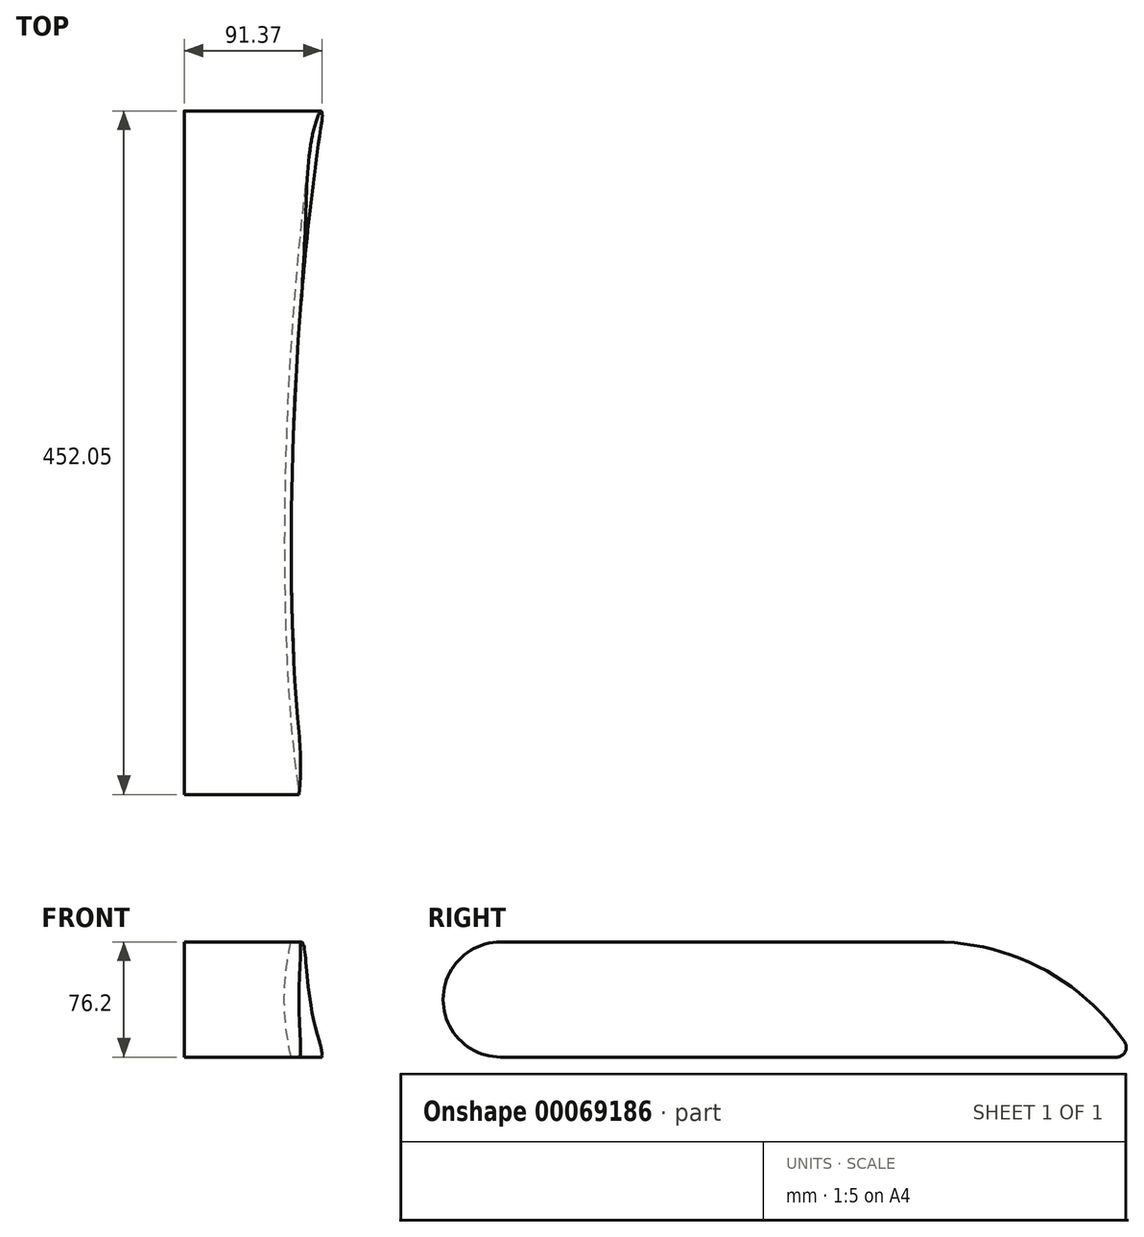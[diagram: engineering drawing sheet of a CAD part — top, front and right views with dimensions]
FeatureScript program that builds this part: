
annotation { "Feature Type Name" : "Feature", "Feature Type Description" : "" }
export const myFeature = defineFeature(function(context is Context, id is Id, definition is map)
    precondition{}
    {
        {
            var Q0;
            Q0=qCreatedBy(makeId("Right.planeOp"),FACE);
            var sketch = newSketch(context, id + "F0", { "sketchPlane" : qUnion([Q0])});
            skFitSpline(sketch, "E0", {"points": [v(0, 125.99) * mm, v(69.38, 151.55) * mm, v(311.86, 161.04) * mm, v(585.01, 131.83) * mm, v(681.42, 98.96) * mm, v(675.58, 90.93) * mm, v(579.9, 116.5) * mm, v(297.25, 149.36) * mm, v(127.81, 148.63) * mm, v(37.98, 131.1) * mm, v(0, 114.3) * mm, v(0, 125.99) * mm]});
            skLineSegment(sketch, "E1", {"start": v(0, 0) * mm, "end": v(154.83, 0) * mm, "construction": true});
            skSolve(sketch);
        }
        {
            var Q0;
            Q0=sQuery(id+"F0.wireOp",EDGE,"E0");
            var Q1;
            Q1=sQuery(id+"F0.wireOp",EDGE,"E1");
            revolve(context, id + "F1", {"bodyType" : ToolBodyType.SURFACE, "surfaceEntities" : qUnion([Q0]), "axis" : qUnion([Q1]), "revolveType" : RevolveType.FULL});
        }
        {
            var Q0;
            Q0=qCreatedBy(makeId("Right.planeOp"),FACE);
            cPlane(context, id + "F2", {"entities" : qUnion([Q0]), "cplaneType" : CPlaneType.OFFSET, "offset" : 228.6 * mm, "oppositeDirection" : true, "width" : 152.4 * mm, "height" : 152.4 * mm});
        }
        {
            var Q0;
            Q0=qCreatedBy(id+"F2.planeOp",FACE);
            var sketch = newSketch(context, id + "F3", { "sketchPlane" : qUnion([Q0])});
            skLineSegment(sketch, "E2.bottom", {"start": v(76.2, 38.1) * mm, "end": v(533.4, 38.1) * mm});
            skLineSegment(sketch, "E2.top", {"start": v(76.2, -38.1) * mm, "end": v(533.4, -38.1) * mm});
            skLineSegment(sketch, "E2.left", {"start": v(76.2, 38.1) * mm, "end": v(76.2, -38.1) * mm});
            skLineSegment(sketch, "E2.right", {"start": v(533.4, 38.1) * mm, "end": v(533.4, -38.1) * mm});
            skSolve(sketch);
        }
        {
            var Q0;
            Q0=makeQuery(id+"F3.imprint","IMPRINT",FACE,{"disambiguationData":[TD([[makeQuery(id+"F3.imprint","IMPRINT",EDGE,{"derivedFrom":sQuery(id+"F3.wireOp",EDGE,"E2.bottom")}),-1.0]])]});
            var Q1;
            Q1=makeQuery(id+"F1.opRevolve","SWEPT_FACE",FACE,{"disambiguationData":[OSD([sQuery(id+"F0.wireOp",EDGE,"E0")])]});
            extrude(context, id + "F4", {"entities" : qUnion([Q0]), "endBound" : BoundingType.UP_TO_SURFACE, "endBoundEntityFace" : qUnion([Q1]), "depth" : 25.4 * mm});
        }
        {
            var Q0;
            Q0=makeQuery(id+"F4.opExtrude","SWEPT_EDGE",EDGE,{"disambiguationData":[OSD([sQuery(id+"F3.wireOp",EDGE,"E2.bottom"),sQuery(id+"F3.wireOp",EDGE,"E2.left")])]});
            var Q1;
            Q1=makeQuery(id+"F4.opExtrude","SWEPT_EDGE",EDGE,{"disambiguationData":[OSD([sQuery(id+"F3.wireOp",EDGE,"E2.top"),sQuery(id+"F3.wireOp",EDGE,"E2.left")])]});
            fillet(context, id + "F5", {"entities" : qUnion([Q0, Q1]), "radius" : 38.1 * mm, "tangentPropagation" : true, "allowEdgeOverflow" : false});
        }
        {
            var Q0;
            Q0=makeQuery(id+"F4.opExtrude","SWEPT_EDGE",EDGE,{"disambiguationData":[OSD([sQuery(id+"F3.wireOp",EDGE,"E2.bottom"),sQuery(id+"F3.wireOp",EDGE,"E2.right")])]});
            fillet(context, id + "F6", {"entities" : qUnion([Q0]), "radius" : 152.4 * mm, "tangentPropagation" : true, "allowEdgeOverflow" : false});
        }
        {
            var Q0;
            Q0=makeQuery(id+"F6.opFillet","BLEND_EDGE",EDGE,{"blendedFrom":[makeQuery(id+"F4.opExtrude","SWEPT_EDGE",EDGE,{"disambiguationData":[OSD([sQuery(id+"F3.wireOp",EDGE,"E2.bottom"),sQuery(id+"F3.wireOp",EDGE,"E2.right")])]}),makeQuery(id+"F4.opExtrude","SWEPT_FACE",FACE,{"disambiguationData":[OSD([sQuery(id+"F3.wireOp",EDGE,"E2.top")])]})],"blendedInto":[makeQuery(id+"F4.opExtrude","SWEPT_FACE",FACE,{"disambiguationData":[OSD([sQuery(id+"F3.wireOp",EDGE,"E2.top")])]})]});
            fillet(context, id + "F7", {"entities" : qUnion([Q0]), "radius" : 6.35 * mm, "tangentPropagation" : true, "allowEdgeOverflow" : false});
        }
    });
